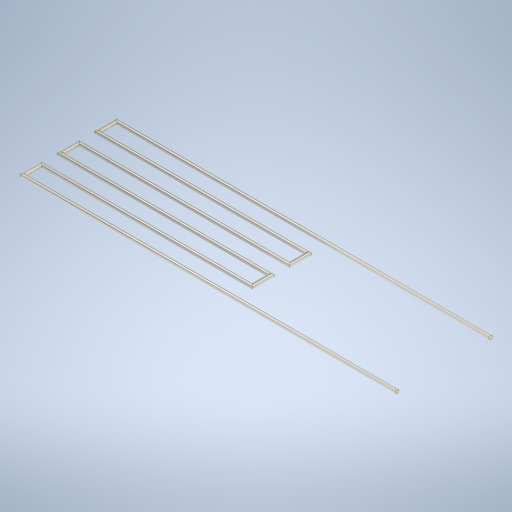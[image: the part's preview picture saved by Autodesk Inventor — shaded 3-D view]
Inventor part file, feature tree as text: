
AUTODESK INVENTOR PART (.ipt)
format: ipt  version: 2024.2 (Build 282272000, 272)  size: 287,232 bytes
history: native  units: in
note: dims shown in document units (in); Inventor stores cm internally (conversion verified against a paired STEP export)
features: sketch x3, plane x2, sweep x1, extrude x1
ambient origin geometry x8: Origin, YZ Plane, XZ Plane, XY Plane, X Axis, Y Axis, Z Axis, Center Point
bodies: Solid1 (feature_tree)
feature tree (7):
  sweep  "Sweep1"
  plane  "Work Plane1"
  plane  "Work Plane2"
  extrude  "Extrusion3"  Depth=0.1in
  sketch  "Sketch1"  dims[d0=1.5in d1=0.1in]
  sketch  "Sketch2"  dims[d2=1.125in d3=0.1in]
  sketch  "Sketch5"  dims[d4=0.05in d5=0.05in d6=0.0in d7=0.0in d8=0.02in d11=0.25in d19=-0.25in d20=0.5in d21=0.0in]
